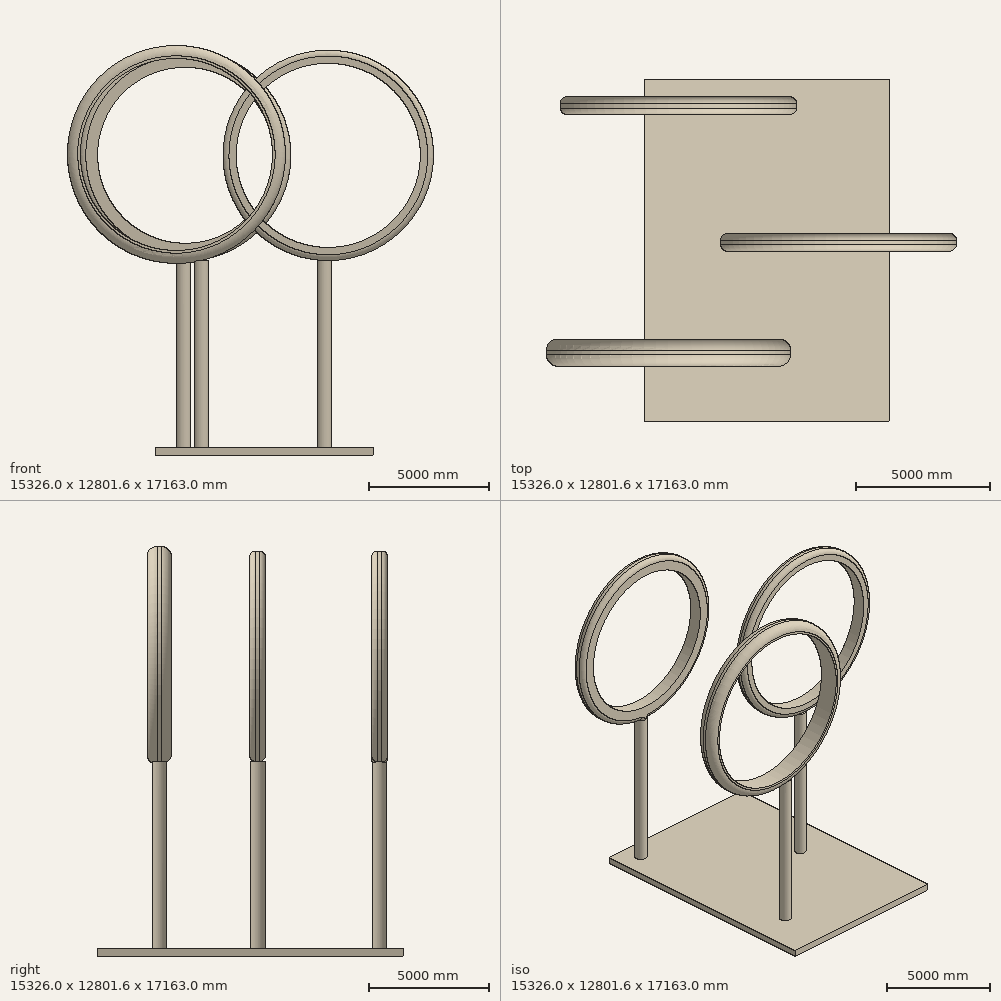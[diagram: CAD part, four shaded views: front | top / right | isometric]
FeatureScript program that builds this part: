
annotation { "Feature Type Name" : "Feature", "Feature Type Description" : "" }
export const myFeature = defineFeature(function(context is Context, id is Id, definition is map)
    precondition{}
    {
        {
            var Q0;
            Q0=qCreatedBy(makeId("Top.planeOp"),FACE);
            var sketch = newSketch(context, id + "F0", { "sketchPlane" : qUnion([Q0])});
            skLineSegment(sketch, "E0.bottom", {"start": v(4572, -6400.8) * mm, "end": v(-4572, -6400.8) * mm});
            skLineSegment(sketch, "E0.top", {"start": v(4572, 6400.8) * mm, "end": v(-4572, 6400.8) * mm});
            skLineSegment(sketch, "E0.left", {"start": v(4572, -6400.8) * mm, "end": v(4572, 6400.8) * mm});
            skLineSegment(sketch, "E0.right", {"start": v(-4572, -6400.8) * mm, "end": v(-4572, 6400.8) * mm});
            skPoint(sketch, "E0.middle", {"position": v(0, 0) * mm});
            skSolve(sketch);
        }
        {
            var Q0;
            Q0=makeQuery(id+"F0.imprint","IMPRINT",FACE,{"disambiguationData":[TD([[makeQuery(id+"F0.imprint","IMPRINT",EDGE,{"derivedFrom":sQuery(id+"F0.wireOp",EDGE,"E0.bottom")}),-1.0]])]});
            extrude(context, id + "F1", {"entities" : qUnion([Q0]), "depth" : 330.2 * mm, "offsetDistance" : 25.4 * mm});
        }
        {
            var Q0;
            Q0=makeQuery(id+"F1.opExtrude","CAP_FACE",FACE,{"disambiguationData":[OSD([sQuery(id+"F0.wireOp",EDGE,"E0.bottom"),sQuery(id+"F0.wireOp",EDGE,"E0.top"),sQuery(id+"F0.wireOp",EDGE,"E0.left"),sQuery(id+"F0.wireOp",EDGE,"E0.right")])],"isStart":false});
            var sketch = newSketch(context, id + "F2", { "sketchPlane" : qUnion([Q0])});
            skSolve(sketch);
        }
        {
            var Q0;
            Q0=makeQuery(id+"F2.imprint","IMPRINT",FACE,{"disambiguationData":[TD([[makeQuery(id+"F2.imprint","IMPRINT",EDGE,{"derivedFrom":makeQuery(id+"F1.opExtrude","CAP_EDGE",EDGE,{"disambiguationData":[OSD([sQuery(id+"F0.wireOp",EDGE,"E0.bottom")])],"isStart":false})}),-1.0]])]});
            var sketch = newSketch(context, id + "F3", { "sketchPlane" : qUnion([Q0])});
            skCircle(sketch, "E1", {"center": v(-3390.72, 5395.09) * mm, "radius": 300.67 * mm});
            skCircle(sketch, "E2", {"center": v(2509.2, 315.89) * mm, "radius": 300.67 * mm});
            skCircle(sketch, "E3", {"center": v(-2646.1, -3808.37) * mm, "radius": 300.67 * mm});
            skSolve(sketch);
        }
        {
            var Q0;
            Q0=makeQuery(id+"F3.imprint","IMPRINT",FACE,{"disambiguationData":[TD([[makeQuery(id+"F3.imprint","IMPRINT",EDGE,{"derivedFrom":sQuery(id+"F3.wireOp",EDGE,"E1")}),1.0]])]});
            var Q1;
            Q1=makeQuery(id+"F3.imprint","IMPRINT",FACE,{"disambiguationData":[TD([[makeQuery(id+"F3.imprint","IMPRINT",EDGE,{"derivedFrom":sQuery(id+"F3.wireOp",EDGE,"E2")}),1.0]])]});
            var Q2;
            Q2=makeQuery(id+"F3.imprint","IMPRINT",FACE,{"disambiguationData":[TD([[makeQuery(id+"F3.imprint","IMPRINT",EDGE,{"derivedFrom":sQuery(id+"F3.wireOp",EDGE,"E3")}),1.0]])]});
            extrude(context, id + "F4", {"entities" : qUnion([Q0, Q1, Q2]), "operationType" : NewBodyOperationType.ADD, "depth" : 7823.2 * mm, "offsetDistance" : 25.4 * mm});
        }
        {
            var Q0;
            Q0=makeQuery(id+"F4.opExtrude","CAP_FACE",FACE,{"disambiguationData":[OSD([sQuery(id+"F3.wireOp",EDGE,"E1")])],"isStart":false});
            var sketch = newSketch(context, id + "F5", { "sketchPlane" : qUnion([Q0])});
            skLineSegment(sketch, "E4", {"start": v(-3691.04, 5409.7) * mm, "end": v(-3090.4, 5409.7) * mm});
            skSolve(sketch);
        }
        {
            var Q0;
            Q0=sQuery(id+"F5.wireOp",EDGE,"E4");
            cPlane(context, id + "F6", {"entities" : qUnion([Q0]), "cplaneType" : CPlaneType.LINE_ANGLE, "offset" : 25.4 * mm, "angle" : 0 * degree, "width" : 152.4 * mm, "height" : 152.4 * mm});
        }
        {
            var Q0;
            Q0=makeQuery(id+"F4.opExtrude","CAP_FACE",FACE,{"disambiguationData":[OSD([sQuery(id+"F3.wireOp",EDGE,"E2")])],"isStart":false});
            var sketch = newSketch(context, id + "F7", { "sketchPlane" : qUnion([Q0])});
            skLineSegment(sketch, "E5", {"start": v(2208.97, 299.74) * mm, "end": v(2809.44, 299.74) * mm});
            skSolve(sketch);
        }
        {
            var Q0;
            Q0=sQuery(id+"F7.wireOp",EDGE,"E5");
            cPlane(context, id + "F8", {"entities" : qUnion([Q0]), "cplaneType" : CPlaneType.LINE_ANGLE, "offset" : 25.4 * mm, "angle" : 0 * degree, "width" : 152.4 * mm, "height" : 152.4 * mm});
        }
        {
            var Q0;
            Q0=makeQuery(id+"F4.opExtrude","CAP_FACE",FACE,{"disambiguationData":[OSD([sQuery(id+"F3.wireOp",EDGE,"E3")])],"isStart":false});
            var sketch = newSketch(context, id + "F9", { "sketchPlane" : qUnion([Q0])});
            skLineSegment(sketch, "E6", {"start": v(-2946.64, -3817.26) * mm, "end": v(-2345.56, -3817.26) * mm});
            skSolve(sketch);
        }
        {
            var Q0;
            Q0=sQuery(id+"F9.wireOp",EDGE,"E6");
            cPlane(context, id + "F10", {"entities" : qUnion([Q0]), "cplaneType" : CPlaneType.LINE_ANGLE, "offset" : 25.4 * mm, "angle" : 0 * degree, "width" : 152.4 * mm, "height" : 152.4 * mm});
        }
        {
            var Q0;
            Q0=qCreatedBy(id+"F6.planeOp",FACE);
            var sketch = newSketch(context, id + "F11", { "sketchPlane" : qUnion([Q0])});
            skCircle(sketch, "E7", {"center": v(3311.8, 12556.25) * mm, "radius": 4418.53 * mm});
            skPoint(sketch, "E7.first.point", {"position": v(2643, 8188.63) * mm});
            skPoint(sketch, "E7.second.point", {"position": v(3030.13, 16965.8) * mm});
            skPoint(sketch, "E7.third.point", {"position": v(4319.44, 16858.35) * mm});
            skSolve(sketch);
        }
        {
            var Q0;
            Q0=makeQuery(id+"F11.imprint","IMPRINT",FACE,{"disambiguationData":[TD([[makeQuery(id+"F11.imprint","IMPRINT",EDGE,{"derivedFrom":sQuery(id+"F11.wireOp",EDGE,"E7")}),1.0]])]});
            var sketch = newSketch(context, id + "F12", { "sketchPlane" : qUnion([Q0])});
            skCircle(sketch, "E8", {"center": v(3305.17, 12564.95) * mm, "radius": 3682.4 * mm});
            skSolve(sketch);
        }
        {
            var Q0;
            Q0=makeQuery(id+"F12.imprint","IMPRINT",FACE,{"disambiguationData":[TD([[makeQuery(id+"F12.imprint","IMPRINT",EDGE,{"derivedFrom":sQuery(id+"F12.wireOp",EDGE,"E8")}),-1.0]])]});
            extrude(context, id + "F13", {"entities" : qUnion([Q0]), "operationType" : NewBodyOperationType.ADD, "endBound" : BoundingType.SYMMETRIC, "depth" : 660.4 * mm, "offsetDistance" : 25.4 * mm});
        }
        {
            var Q0;
            Q0=makeQuery(id+"F13.opExtrude","CAP_EDGE",EDGE,{"disambiguationData":[OSD([sQuery(id+"F11.wireOp",EDGE,"E7")])],"isStart":false});
            var Q1;
            Q1=makeQuery(id+"F13.opExtrude","CAP_EDGE",EDGE,{"disambiguationData":[OSD([sQuery(id+"F11.wireOp",EDGE,"E7")])],"isStart":true});
            fillet(context, id + "F14", {"entities" : qUnion([Q0, Q1]), "radius" : 245.28 * mm, "tangentPropagation" : true, "allowEdgeOverflow" : false});
        }
        {
            var Q0;
            Q0=qCreatedBy(id+"F8.planeOp",FACE);
            var sketch = newSketch(context, id + "F15", { "sketchPlane" : qUnion([Q0])});
            skCircle(sketch, "E9", {"center": v(-2670.69, 12561.06) * mm, "radius": 4406.65 * mm});
            skPoint(sketch, "E9.first.point", {"position": v(-2516.03, 8157.13) * mm});
            skPoint(sketch, "E9.second.point", {"position": v(-2484.01, 16963.76) * mm});
            skPoint(sketch, "E9.third.point", {"position": v(270.06, 15842.92) * mm});
            skCircle(sketch, "E10", {"center": v(-2670.69, 12561.06) * mm, "radius": 3853.9 * mm});
            skSolve(sketch);
        }
        {
            var Q0;
            Q0=makeQuery(id+"F15.imprint","IMPRINT",FACE,{"disambiguationData":[TD([[makeQuery(id+"F15.imprint","IMPRINT",EDGE,{"derivedFrom":sQuery(id+"F15.wireOp",EDGE,"E9")}),1.0]])]});
            extrude(context, id + "F16", {"entities" : qUnion([Q0]), "endBound" : BoundingType.SYMMETRIC, "depth" : 660.4 * mm, "offsetDistance" : 25.4 * mm});
        }
        {
            var Q0;
            Q0=makeQuery(id+"F16.opExtrude","CAP_EDGE",EDGE,{"disambiguationData":[OSD([sQuery(id+"F15.wireOp",EDGE,"E9")])],"isStart":true});
            var Q1;
            Q1=makeQuery(id+"F16.opExtrude","CAP_EDGE",EDGE,{"disambiguationData":[OSD([sQuery(id+"F15.wireOp",EDGE,"E9")])],"isStart":false});
            fillet(context, id + "F17", {"entities" : qUnion([Q0, Q1]), "radius" : 245.29 * mm, "tangentPropagation" : true, "allowEdgeOverflow" : false});
        }
        {
            var Q0;
            Q0=qCreatedBy(id+"F10.planeOp",FACE);
            var sketch = newSketch(context, id + "F18", { "sketchPlane" : qUnion([Q0])});
            skCircle(sketch, "E11", {"center": v(3685.87, 12600.22) * mm, "radius": 4562.76 * mm});
            skPoint(sketch, "E11.first.point", {"position": v(2658.6, 8154.6) * mm});
            skPoint(sketch, "E11.second.point", {"position": v(2419.02, 16983.58) * mm});
            skPoint(sketch, "E11.third.point", {"position": v(2069.33, 16867.02) * mm});
            skCircle(sketch, "E12", {"center": v(3685.87, 12600.22) * mm, "radius": 4021.7 * mm});
            skSolve(sketch);
        }
        {
            var Q0;
            Q0=makeQuery(id+"F18.imprint","IMPRINT",FACE,{"disambiguationData":[TD([[makeQuery(id+"F18.imprint","IMPRINT",EDGE,{"derivedFrom":sQuery(id+"F18.wireOp",EDGE,"E11")}),1.0]])]});
            extrude(context, id + "F19", {"entities" : qUnion([Q0]), "operationType" : NewBodyOperationType.ADD, "endBound" : BoundingType.SYMMETRIC, "depth" : 1016 * mm, "offsetDistance" : 25.4 * mm});
        }
        {
            var Q0;
            Q0=makeQuery(id+"F19.opExtrude","CAP_EDGE",EDGE,{"disambiguationData":[OSD([sQuery(id+"F18.wireOp",EDGE,"E11")])],"isStart":true});
            var Q1;
            Q1=makeQuery(id+"F19.opExtrude","CAP_EDGE",EDGE,{"disambiguationData":[OSD([sQuery(id+"F18.wireOp",EDGE,"E11")])],"isStart":false});
            fillet(context, id + "F20", {"entities" : qUnion([Q0, Q1]), "radius" : 429.25 * mm, "tangentPropagation" : true, "allowEdgeOverflow" : false});
        }
    });
